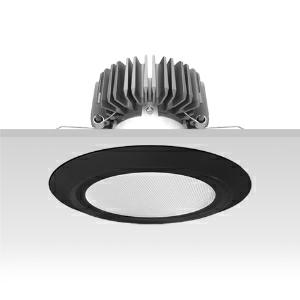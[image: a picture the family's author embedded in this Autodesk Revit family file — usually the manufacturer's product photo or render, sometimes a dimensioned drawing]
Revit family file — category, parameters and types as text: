
# Revit family: 3f_filippi_-_3f_reno_bianco_ampio_3f_filippi_-_30629_a01049_-_3f_reno_200_wh_3000-840_wide___smp_bk_93f3
name_source: partatom
category: Lighting Fixtures
units: mm (PartAtom-declared; Revit-internal decimal feet)

## family parameters
Cut with Voids When Loaded = No
Host = Face
Light Source = No
Part Type = Normal
Room Calculation Point = No
Round Connector Dimension = Use Diameter
Shared = No

## types (1)
- 3F Filippi - 3F Reno Bianco Ampio (1 x LED, 2312 lm, 28 W, 4000 K)
    Apparent Load = 28 VA
    Approval mark = CE
    CIE Flux Codes = 74 92 98 100 100
    Color Rendering = 80
    Color Temperature = 4000 K
    Control Gear = Electronic ballast
    Default Elevation = 1800 mm
    Description = ILLUMINOTECHNICAL
Luminous efficiency 100% (DLOR 100%, ULOR 0%).
Initial luminous flux of the luminaire 2312 lm.
Direct symmetric wide distribution.
Installation Interdistance Transv.D = 1.06 x hu - Long.D = 1.04 x hu.
Tabular UGR (CIE 117 - 4H-8H; S=0.25H; 70/50/20): RUG 22.5 - 22.3.
Beam angle: 70° - 69°.
Luminous efficacy 83 lm/W.
Lifetime (L90/B10): 30000 h. (tq+25°C)
Lifetime (L85/B10): 50000 h. (tq+25°C)
Lifetime (L70/B10): 80000 h. (tq+25°C)
Sudden decreased luminous flux after 50000 hours: 0% (C0).
Photobiological safety in compliance with IEC/TR 62778: RG0 risk exempt, (IEC 62471).
In compliance with IEC/EN 62722-2-1 - IEC/EN 62717 standards.

SOURCE
Compact LED module 3000/840.
Energy efficiency class (UE 2019/2020 - UE 2019/2015): D.
CIE 13.3 Colour rendering index: CRI >80 (R9 <50%).
IES TM-30 Fidelity Index: Rf = 84 Rg = 95.
CCT nominal colour temperature 4000 K.
Colour initial tolerance (MacAdam): SDCM 3.
Zhaga Book 3 compliant.

MECHANICAL
Passive heat dissipator in die-casting aluminium, oversized, for optimum thermal management of the LED module.
Parabolic element with graduated/concentric rings in white polycarbonate.
Transparent external lens with glossy and satin differentiated surfaces, with a cooling and anti-insect system in methacrylate (PMMA).
Fastening spring clips in stainless steel.
Dimensions: diameter 226 mm, height 146 mm. Weight 1.63 kg.
IP44 protection degree for exposed part, IP20 for recessed part.
Mechanical strength to impacts IK05 (0.7 joule).
Glow-wire test resistance 650°C.

ELECTRICAL
Wiring on a separate unit.
Halogen Free electronic wiring 230V-50/60Hz, power factor 0.95, THD <25%, constant output current, SELV, class II, 1 driver.
Power of the luminaire 28 W.
ENEC - CE.
SAFE FLICKER: PstLM=<1 and SVM=<0.4 (IEC TR 61547-1 and IEC TR 63158), to ensure a more comfortable and safe light.
Luminaire compliant with EN 60598-2-22 for power supply from a centralised emergency system CPSS (Central Power Supply System), not incorporated in the luminaire - high risk areas excluded. The default power and flux are 100% in AC and 100% in DC.
Ambient temperature from 0°C to +25°C.
Temperature class T6 max 85°C.
Relative humidity UR: <85%.

INSTALLATION
Pull-up recessed fitting.
False ceiling carving: 200 mm.
All accessories dedicated to this product are available on the Catalog and on our website www.3F-Filippi.com.

ACCESSORIES
A01049 - Anti-glare microprismatic SMP diffuser in methacrylate (PMMA), locked and in line with the trim, in black polycarbonate.

APPLICATIONS
Suitable product for food production plants (HACCP), IFS (Food Version 6), BRC (GSFS Food Version 7).
Environments: architectural, commercial, exhibition areas, transit areas, corridors, shops, display windows, service areas.
In false ceilings with narrow voids.

WARNING
Luminaire designed for disposal/recycling at end-of-life.
Replaceable (LED only) light source by a professional. Replaceable control gear by a professional.
    Height = 0 mm  [stored 0 ft]
    Lamp = 1 x LED
    Lamp Light Flux = 2312 lm
    Lamp Power = 28 W
    Lamp count = 1
    Length = 226 mm
    Lifetime = 50000 h
    Luminous efficacy = 83 lm/W
    Manufacturer = 3F Filippi
    ModVariant = No
    Model = 3F Filippi - 30629+A01049 - 3F Reno 200 WH 3000-840 WIDE + SMP BK
    Mounting Place = Ceiling
    Mounting Type = Recessed
    Number of Poles = 1
    OnlyDefault = Yes
    Power Factor = 1
    Product Name = 3F Filippi - 3F Reno Bianco Ampio
    Product group = recessed luminaire
    ProductGroupID = 4
    Protection Class = Protection class II
    Protection Degree = IP 20
    RLX_Detail_Level = 1
    RLX_Emergency_Light_Flux = 0 lm
    RLX_Emergency_Type = 0
    RLX_Emergency_Type_DB = No
    RlxData = <blob elided: 97833 chars, md5=07b1983c>
    Socket = socket
    Standby Power = 0 W
    System Light Flux = 2312 lm
    System Power = 28 W
    Type Comments = Product without accessories
    Type Image = 3ffilippi_3f_reno_200_bk_vs_smp.jpg
    URL = http://relux.com
    VarID = ---
    Voltage = 0 V
    Weight = 0.00 kg
    Width = 0 mm  [stored 0 ft]

note: [stored X ft] marks values corroborated as IEEE doubles in the binary element streams (Revit-internal decimal feet)

## geometry (parser evidence)
native form markers: Blend x4, Sweep x11
no freeform markers — native parametric forms only
